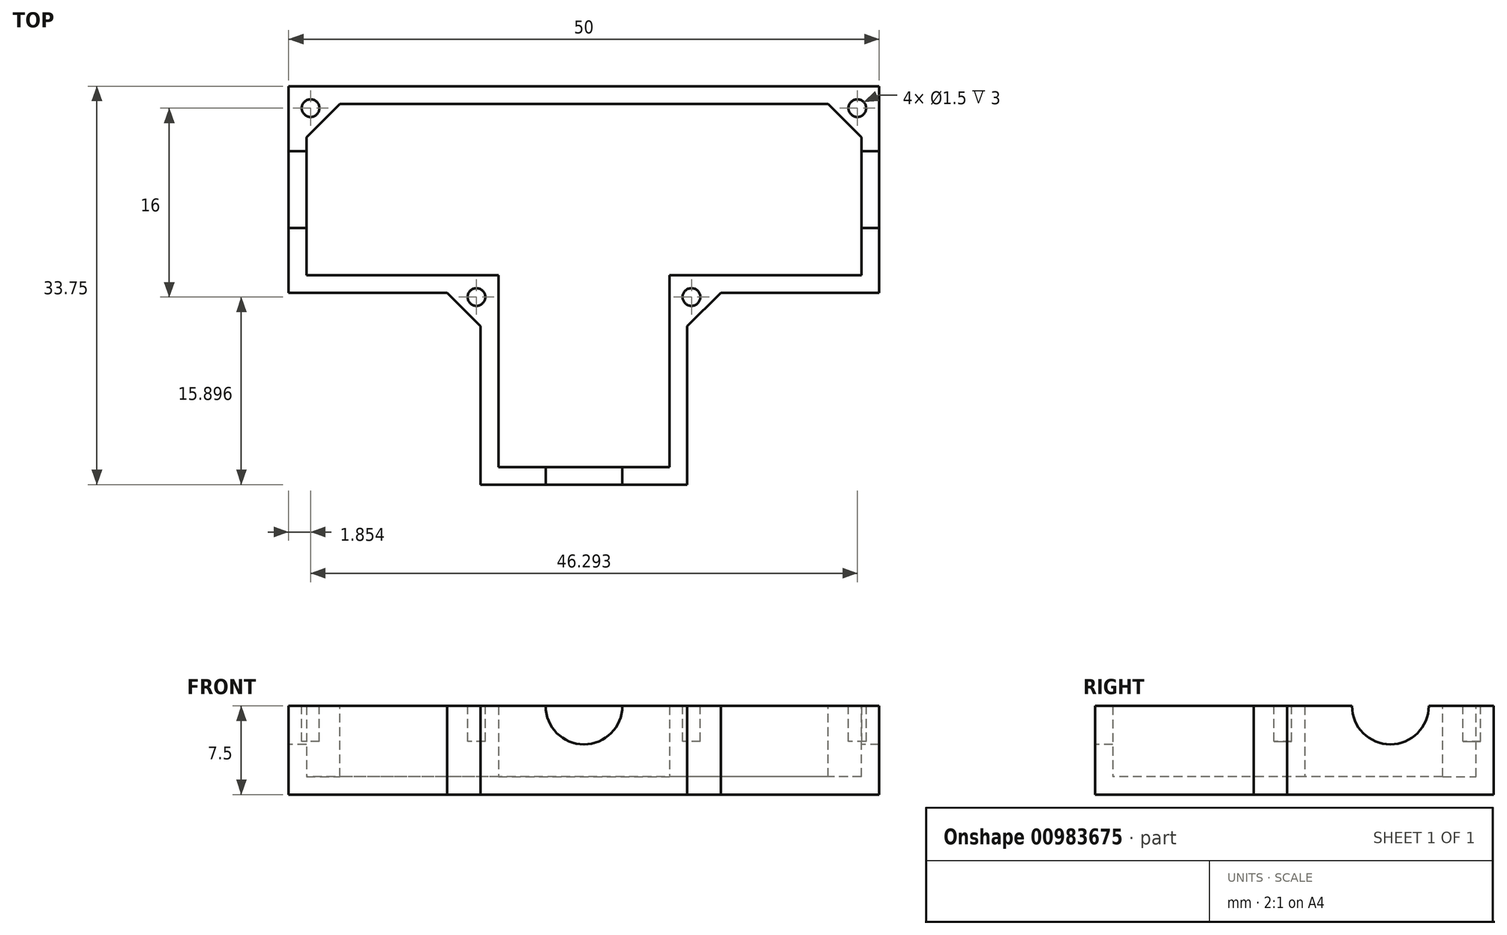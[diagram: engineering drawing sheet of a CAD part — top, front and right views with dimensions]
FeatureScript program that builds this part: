
annotation { "Feature Type Name" : "Feature", "Feature Type Description" : "" }
export const myFeature = defineFeature(function(context is Context, id is Id, definition is map)
    precondition{}
    {
        {
            var Q0;
            Q0=qCreatedBy(makeId("Top.planeOp"),FACE);
            var sketch = newSketch(context, id + "F0", { "sketchPlane" : qUnion([Q0])});
            skLineSegment(sketch, "E0.bottom", {"start": v(25, 8.75) * mm, "end": v(8.75, 8.75) * mm});
            skLineSegment(sketch, "E0.top", {"start": v(25, -8.75) * mm, "end": v(8.75, -8.75) * mm});
            skLineSegment(sketch, "E0.left", {"start": v(25, 8.75) * mm, "end": v(25, -8.75) * mm});
            skLineSegment(sketch, "E0.right", {"start": v(-25, 8.75) * mm, "end": v(-25, -8.75) * mm});
            skPoint(sketch, "E0.middle", {"position": v(0, 0) * mm});
            skLineSegment(sketch, "E1.top", {"start": v(-8.75, -25) * mm, "end": v(8.75, -25) * mm});
            skLineSegment(sketch, "E2.trimOffspring", {"start": v(-8.75, 8.75) * mm, "end": v(-25, 8.75) * mm});
            skLineSegment(sketch, "E3.trimOffspring", {"start": v(-8.75, -8.75) * mm, "end": v(-8.75, -25) * mm});
            skLineSegment(sketch, "E4.trimOffspring", {"start": v(-8.75, -8.75) * mm, "end": v(-25, -8.75) * mm});
            skLineSegment(sketch, "E5.trimOffspring", {"start": v(8.75, -8.75) * mm, "end": v(8.75, -25) * mm});
            skLineSegment(sketch, "E6", {"start": v(8.75, 8.75) * mm, "end": v(-8.75, 8.75) * mm});
            skLineSegment(sketch, "E7", {"start": v(0, 0) * mm, "end": v(0, -25) * mm});
            skSolve(sketch);
        }
        {
            var Q0;
            Q0=qSketchRegion(id+"F0",true);
            extrude(context, id + "F1", {"entities" : qUnion([Q0]), "depth" : 7.5 * mm, "offsetDistance" : 25 * mm});
        }
        {
            var Q0;
            Q0=makeQuery(id+"F1.opExtrude","CAP_FACE",FACE,{"disambiguationData":[OSD([sQuery(id+"F0.wireOp",EDGE,"E0.bottom"),sQuery(id+"F0.wireOp",EDGE,"E0.top"),sQuery(id+"F0.wireOp",EDGE,"E0.left"),sQuery(id+"F0.wireOp",EDGE,"E0.right"),sQuery(id+"F0.wireOp",EDGE,"E1.bottom"),sQuery(id+"F0.wireOp",EDGE,"E1.top"),sQuery(id+"F0.wireOp",EDGE,"E1.left"),sQuery(id+"F0.wireOp",EDGE,"E1.right"),sQuery(id+"F0.wireOp",EDGE,"E2.trimOffspring"),sQuery(id+"F0.wireOp",EDGE,"E3.trimOffspring"),sQuery(id+"F0.wireOp",EDGE,"E4.trimOffspring"),sQuery(id+"F0.wireOp",EDGE,"E5.trimOffspring")])],"isStart":false});
            shell(context, id + "F2", {"entities" : qUnion([Q0]), "thickness" : 1.5 * mm});
        }
        {
            var Q0;
            Q0=makeQuery(id+"F1.opExtrude","CAP_FACE",FACE,{"disambiguationData":[OSD([sQuery(id+"F0.wireOp",EDGE,"E0.bottom"),sQuery(id+"F0.wireOp",EDGE,"E0.top"),sQuery(id+"F0.wireOp",EDGE,"E0.left"),sQuery(id+"F0.wireOp",EDGE,"E0.right"),sQuery(id+"F0.wireOp",EDGE,"E1.top"),sQuery(id+"F0.wireOp",EDGE,"E2.trimOffspring"),sQuery(id+"F0.wireOp",EDGE,"E3.trimOffspring"),sQuery(id+"F0.wireOp",EDGE,"E4.trimOffspring"),sQuery(id+"F0.wireOp",EDGE,"E5.trimOffspring"),sQuery(id+"F0.wireOp",EDGE,"E6")])],"isStart":false});
            var sketch = newSketch(context, id + "F3", { "sketchPlane" : qUnion([Q0])});
            skLineSegment(sketch, "E8", {"start": v(-23.5, 4.42) * mm, "end": v(-20.67, 7.25) * mm});
            skLineSegment(sketch, "E9", {"start": v(-20.67, 7.25) * mm, "end": v(-23.5, 7.25) * mm});
            skLineSegment(sketch, "E10", {"start": v(-23.5, 7.25) * mm, "end": v(-23.5, 4.42) * mm});
            skLineSegment(sketch, "E11", {"start": v(0, 7.25) * mm, "end": v(0, 0) * mm});
            skLineSegment(sketch, "E12", {"start": v(-11.58, -8.75) * mm, "end": v(-8.75, -8.75) * mm});
            skLineSegment(sketch, "E13", {"start": v(-8.75, -8.75) * mm, "end": v(-8.75, -11.58) * mm});
            skLineSegment(sketch, "E14", {"start": v(-8.75, -11.58) * mm, "end": v(-11.58, -8.75) * mm});
            skLineSegment(sketch, "E15.MirrorCS", {"start": v(20.67, 7.25) * mm, "end": v(23.5, 7.25) * mm});
            skLineSegment(sketch, "E16.MirrorCS", {"start": v(11.58, -8.75) * mm, "end": v(8.75, -8.75) * mm});
            skLineSegment(sketch, "E17.MirrorCS", {"start": v(23.5, 4.42) * mm, "end": v(20.67, 7.25) * mm});
            skLineSegment(sketch, "E18.MirrorCS", {"start": v(8.75, -11.58) * mm, "end": v(11.58, -8.75) * mm});
            skLineSegment(sketch, "E19.MirrorCS", {"start": v(23.5, 7.25) * mm, "end": v(23.5, 4.42) * mm});
            skLineSegment(sketch, "E20.MirrorCS", {"start": v(8.75, -8.75) * mm, "end": v(8.75, -11.58) * mm});
            skSolve(sketch);
        }
        {
            var Q0;
            Q0 = qSketchRegion(id + "F3", true);
            var Q1;
            Q1=makeQuery(id+"F1.opExtrude","CAP_FACE",FACE,{"disambiguationData":[OSD([sQuery(id+"F0.wireOp",EDGE,"E0.bottom"),sQuery(id+"F0.wireOp",EDGE,"E0.top"),sQuery(id+"F0.wireOp",EDGE,"E0.left"),sQuery(id+"F0.wireOp",EDGE,"E0.right"),sQuery(id+"F0.wireOp",EDGE,"E1.top"),sQuery(id+"F0.wireOp",EDGE,"E2.trimOffspring"),sQuery(id+"F0.wireOp",EDGE,"E3.trimOffspring"),sQuery(id+"F0.wireOp",EDGE,"E4.trimOffspring"),sQuery(id+"F0.wireOp",EDGE,"E5.trimOffspring"),sQuery(id+"F0.wireOp",EDGE,"E6")])],"isStart":true});
            extrude(context, id + "F4", {"entities" : qUnion([Q0]), "operationType" : NewBodyOperationType.ADD, "endBound" : BoundingType.UP_TO_SURFACE, "oppositeDirection" : true, "depth" : 25 * mm, "endBoundEntityFace" : qUnion([Q1]), "offsetDistance" : 25 * mm});
        }
        {
            var Q0;
            Q0=makeQuery(id+"F4.boolean.opBoolean","MERGE",FACE,{"derivedFrom":[makeQuery(id+"F1.opExtrude","CAP_FACE",FACE,{"disambiguationData":[OSD([sQuery(id+"F0.wireOp",EDGE,"E0.bottom"),sQuery(id+"F0.wireOp",EDGE,"E0.top"),sQuery(id+"F0.wireOp",EDGE,"E0.left"),sQuery(id+"F0.wireOp",EDGE,"E0.right"),sQuery(id+"F0.wireOp",EDGE,"E1.top"),sQuery(id+"F0.wireOp",EDGE,"E2.trimOffspring"),sQuery(id+"F0.wireOp",EDGE,"E3.trimOffspring"),sQuery(id+"F0.wireOp",EDGE,"E4.trimOffspring"),sQuery(id+"F0.wireOp",EDGE,"E5.trimOffspring"),sQuery(id+"F0.wireOp",EDGE,"E6")])],"isStart":false}),makeQuery(id+"F4.opExtrude","CAP_FACE",FACE,{"disambiguationData":[OSD([sQuery(id+"F3.wireOp",EDGE,"E8"),sQuery(id+"F3.wireOp",EDGE,"E9"),sQuery(id+"F3.wireOp",EDGE,"E10")])],"isStart":true}),makeQuery(id+"F4.opExtrude","CAP_FACE",FACE,{"disambiguationData":[OSD([sQuery(id+"F3.wireOp",EDGE,"E12"),sQuery(id+"F3.wireOp",EDGE,"E13"),sQuery(id+"F3.wireOp",EDGE,"E14")])],"isStart":true}),makeQuery(id+"F4.opExtrude","CAP_FACE",FACE,{"disambiguationData":[OSD([sQuery(id+"F3.wireOp",EDGE,"E15.MirrorCS"),sQuery(id+"F3.wireOp",EDGE,"E17.MirrorCS"),sQuery(id+"F3.wireOp",EDGE,"E19.MirrorCS")])],"isStart":true}),makeQuery(id+"F4.opExtrude","CAP_FACE",FACE,{"disambiguationData":[OSD([sQuery(id+"F3.wireOp",EDGE,"E16.MirrorCS"),sQuery(id+"F3.wireOp",EDGE,"E18.MirrorCS"),sQuery(id+"F3.wireOp",EDGE,"E20.MirrorCS")])],"isStart":true})]});
            var sketch = newSketch(context, id + "F5", { "sketchPlane" : qUnion([Q0])});
            skCircle(sketch, "E21", {"center": v(-9.1, -9.1) * mm, "radius": 0.75 * mm});
            skCircle(sketch, "E22", {"center": v(-23.15, 6.9) * mm, "radius": 0.75 * mm});
            skCircle(sketch, "E23", {"center": v(9.1, -9.1) * mm, "radius": 0.75 * mm});
            skCircle(sketch, "E24", {"center": v(23.15, 6.9) * mm, "radius": 0.75 * mm});
            skLineSegment(sketch, "E25", {"start": v(-9.1, -9.1) * mm, "end": v(-10.16, -10.16) * mm});
            skLineSegment(sketch, "E26", {"start": v(9.1, -9.1) * mm, "end": v(10.16, -10.16) * mm});
            skLineSegment(sketch, "E27", {"start": v(23.15, 6.9) * mm, "end": v(22.09, 5.84) * mm});
            skLineSegment(sketch, "E28", {"start": v(-23.15, 6.9) * mm, "end": v(-22.09, 5.84) * mm});
            skSolve(sketch);
        }
        {
            var Q0;
            Q0 = qSketchRegion(id + "F5", true);
            extrude(context, id + "F6", {"entities" : qUnion([Q0]), "operationType" : NewBodyOperationType.REMOVE, "oppositeDirection" : true, "depth" : 3 * mm, "offsetDistance" : 25 * mm});
        }
        {
            var Q0;
            Q0=makeQuery(id+"F1.opExtrude","SWEPT_FACE",FACE,{"disambiguationData":[OSD([sQuery(id+"F0.wireOp",EDGE,"E1.top")])]});
            var sketch = newSketch(context, id + "F7", { "sketchPlane" : qUnion([Q0])});
            skCircle(sketch, "E29", {"center": v(0, 7.5) * mm, "radius": 3.25 * mm});
            skSolve(sketch);
        }
        {
            var Q0;
            Q0 = qSketchRegion(id + "F7", true);
            var Q1;
            Q1=makeQuery(id+"F2.opShell","OFFSET_FACE",FACE,{"disambiguationData":[OSD([sQuery(id+"F0.wireOp",EDGE,"E0.bottom"),sQuery(id+"F0.wireOp",EDGE,"E2.trimOffspring"),sQuery(id+"F0.wireOp",EDGE,"E6")])]});
            extrude(context, id + "F8", {"entities" : qUnion([Q0]), "operationType" : NewBodyOperationType.REMOVE, "endBound" : BoundingType.UP_TO_SURFACE, "oppositeDirection" : true, "depth" : 25 * mm, "endBoundEntityFace" : qUnion([Q1]), "offsetDistance" : 25 * mm});
        }
        {
            var Q0;
            Q0=makeQuery(id+"F1.opExtrude","SWEPT_FACE",FACE,{"disambiguationData":[OSD([sQuery(id+"F0.wireOp",EDGE,"E0.right")])]});
            var sketch = newSketch(context, id + "F9", { "sketchPlane" : qUnion([Q0])});
            skCircle(sketch, "E30", {"center": v(0, 7.5) * mm, "radius": 3.25 * mm});
            skSolve(sketch);
        }
        {
            var Q0;
            Q0 = qSketchRegion(id + "F9", true);
            extrude(context, id + "F10", {"entities" : qUnion([Q0]), "operationType" : NewBodyOperationType.REMOVE, "endBound" : BoundingType.THROUGH_ALL, "oppositeDirection" : true, "depth" : 25 * mm, "offsetDistance" : 25 * mm});
        }
    });
